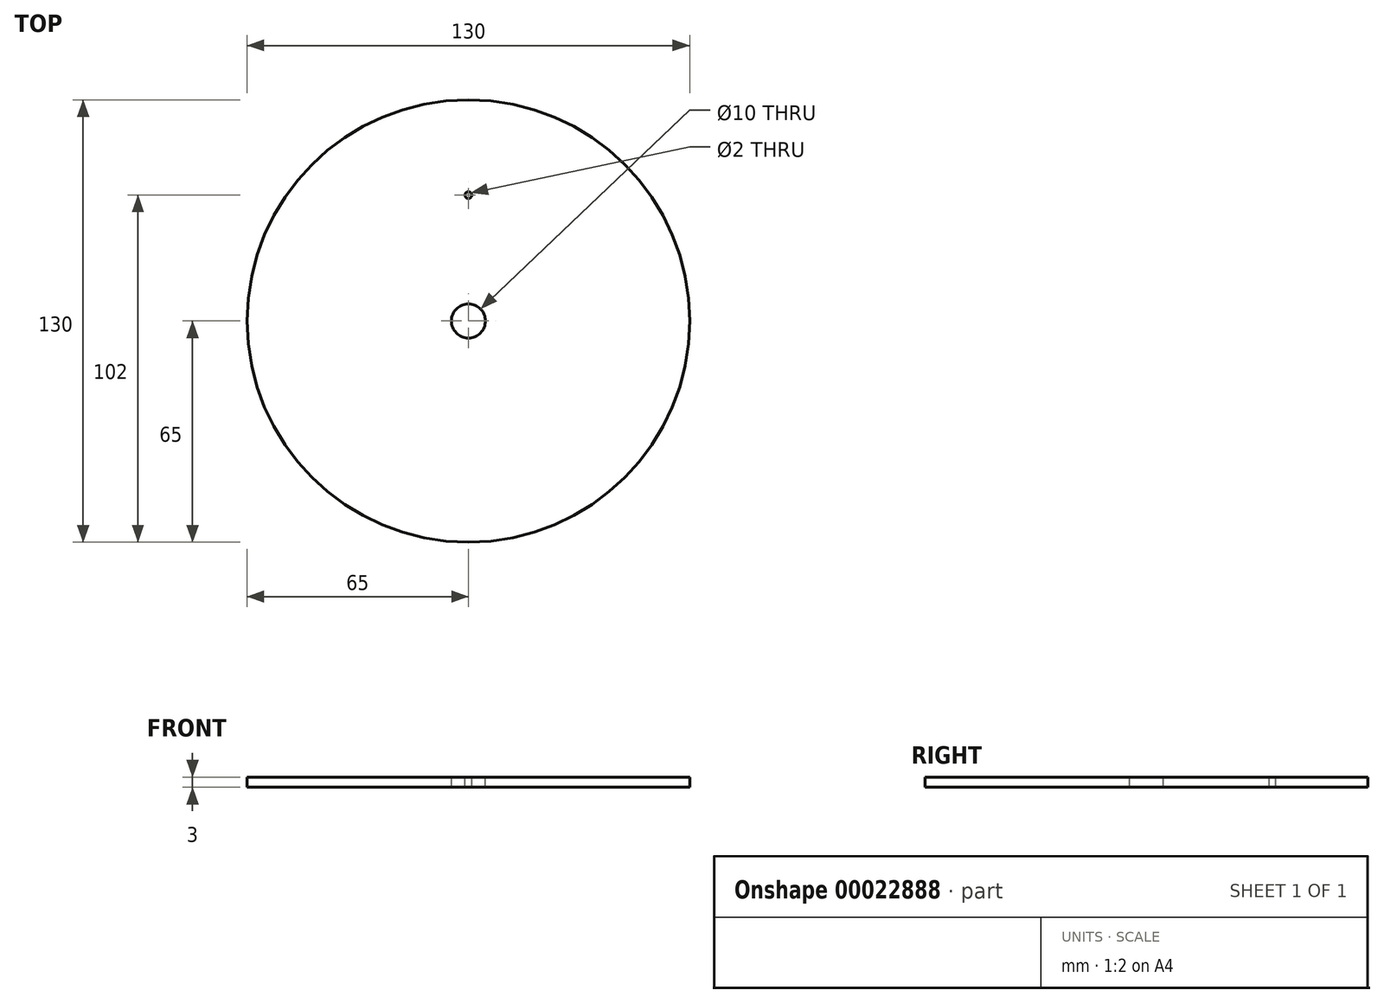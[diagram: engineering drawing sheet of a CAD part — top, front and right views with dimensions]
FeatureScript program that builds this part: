
annotation { "Feature Type Name" : "Feature", "Feature Type Description" : "" }
export const myFeature = defineFeature(function(context is Context, id is Id, definition is map)
    precondition{}
    {
        {
            var Q0;
            Q0=qCreatedBy(makeId("Top.planeOp"),FACE);
            var sketch = newSketch(context, id + "F0", { "sketchPlane" : qUnion([Q0])});
            skCircle(sketch, "E0", {"center": v(0, 0) * mm, "radius": 65 * mm});
            skSolve(sketch);
        }
        {
            var Q0;
            Q0=makeQuery(id+"F0.imprint","IMPRINT",FACE,{"disambiguationData":[TD([[makeQuery(id+"F0.imprint","IMPRINT",EDGE,{"derivedFrom":sQuery(id+"F0.wireOp",EDGE,"E0")}),1.0]])]});
            extrude(context, id + "F1", {"entities" : qUnion([Q0]), "depth" : 3 * mm});
        }
        {
            var Q0;
            Q0=makeQuery(id+"F1.opExtrude","CAP_FACE",FACE,{"disambiguationData":[OSD([sQuery(id+"F0.wireOp",EDGE,"E0")])],"isStart":false});
            var sketch = newSketch(context, id + "F2", { "sketchPlane" : qUnion([Q0])});
            skPoint(sketch, "E1", {"position": v(0, 0) * mm});
            skSolve(sketch);
        }
        {
            var Q0;
            Q0=sQuery(id+"F2.wireOp",VERTEX,"E1");
            var Q1;
            Q1=makeQuery(id+"F1.opExtrude","SWEPT_BODY",BODY,{"disambiguationData":[OSD([sQuery(id+"F0.wireOp",EDGE,"E0")])]});
            hole(context, id + "F3", {"style" : HoleStyle.SIMPLE, "holeDiameter" : 10 * mm, "endStyle" : HoleEndStyle.THROUGH, "locations" : qUnion([Q0]), "scope" : qUnion([Q1])});
        }
        {
            var Q0;
            Q0=makeQuery(id+"F1.opExtrude","CAP_FACE",FACE,{"disambiguationData":[OSD([sQuery(id+"F0.wireOp",EDGE,"E0")])],"isStart":false});
            var sketch = newSketch(context, id + "F4", { "sketchPlane" : qUnion([Q0])});
            skPoint(sketch, "E2", {"position": v(0, 37) * mm});
            skSolve(sketch);
        }
        {
            var Q0;
            Q0=sQuery(id+"F4.wireOp",VERTEX,"E2");
            var Q1;
            Q1=makeQuery(id+"F1.opExtrude","SWEPT_BODY",BODY,{"disambiguationData":[OSD([sQuery(id+"F0.wireOp",EDGE,"E0")])]});
            hole(context, id + "F5", {"style" : HoleStyle.SIMPLE, "holeDiameter" : 2 * mm, "endStyle" : HoleEndStyle.THROUGH, "locations" : qUnion([Q0]), "scope" : qUnion([Q1])});
        }
    });
